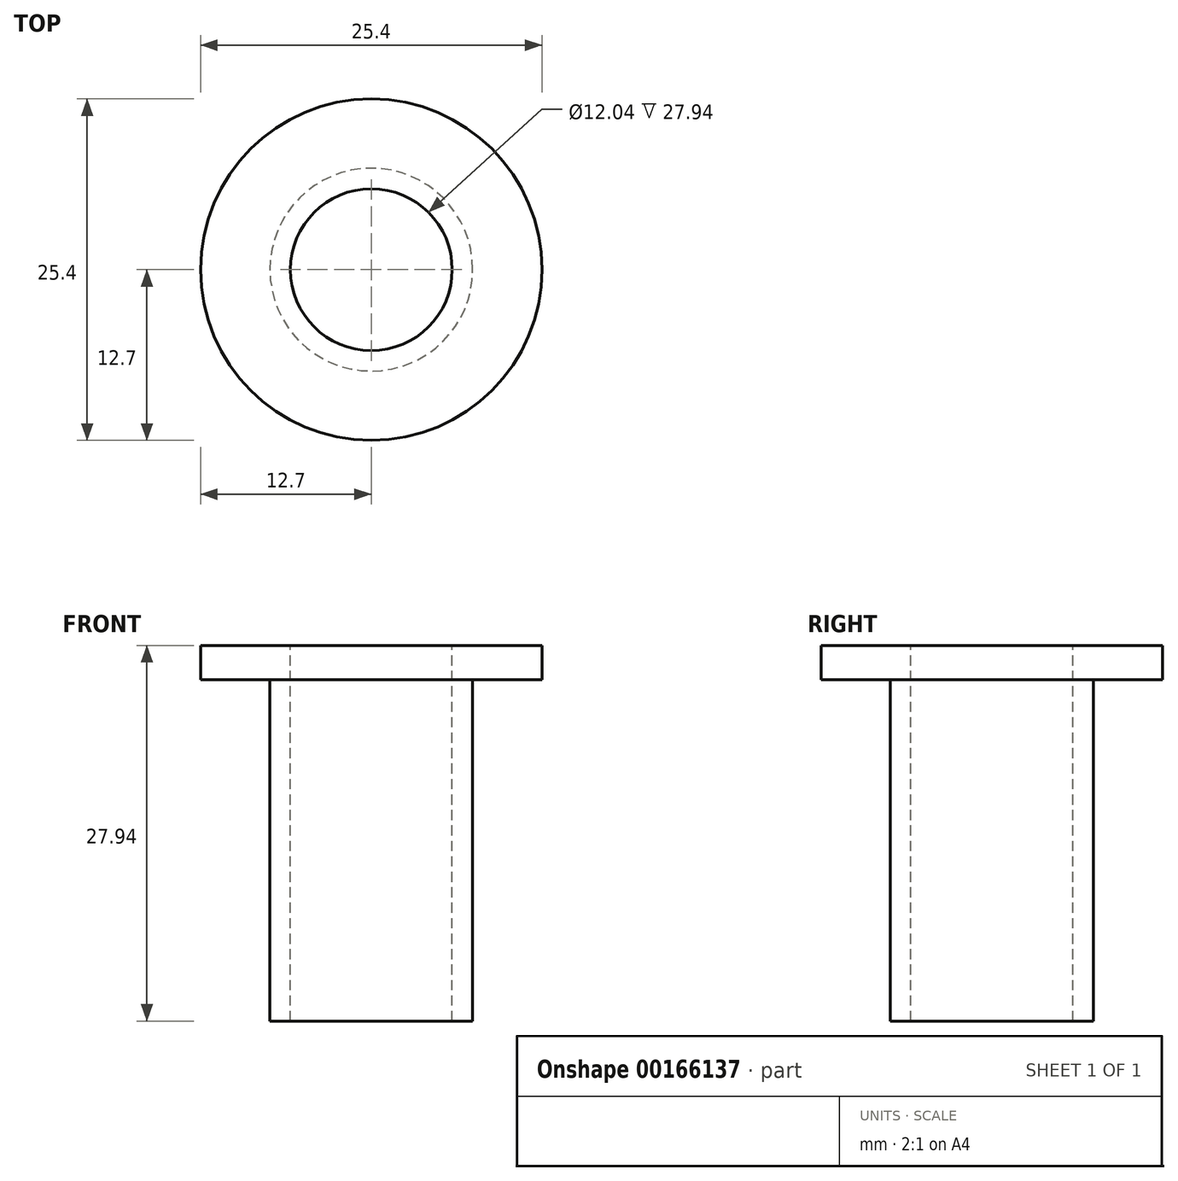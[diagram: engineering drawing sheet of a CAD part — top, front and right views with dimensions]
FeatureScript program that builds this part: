
annotation { "Feature Type Name" : "Feature", "Feature Type Description" : "" }
export const myFeature = defineFeature(function(context is Context, id is Id, definition is map)
    precondition{}
    {
        {
            var Q0;
            Q0=qCreatedBy(makeId("Front.planeOp"),FACE);
            var sketch = newSketch(context, id + "F0", { "sketchPlane" : qUnion([Q0])});
            skLineSegment(sketch, "E0", {"start": v(7.54, 0) * mm, "end": v(7.54, -25.4) * mm});
            skLineSegment(sketch, "E1", {"start": v(7.54, -25.4) * mm, "end": v(6.02, -25.4) * mm});
            skLineSegment(sketch, "E2", {"start": v(6.02, -25.4) * mm, "end": v(6.02, 2.54) * mm});
            skLineSegment(sketch, "E3", {"start": v(6.02, 2.54) * mm, "end": v(12.7, 2.54) * mm});
            skLineSegment(sketch, "E4", {"start": v(12.7, 2.54) * mm, "end": v(12.7, 0) * mm});
            skLineSegment(sketch, "E5", {"start": v(12.7, 0) * mm, "end": v(7.54, 0) * mm});
            skLineSegment(sketch, "E6", {"start": v(0, 11.06) * mm, "end": v(0, -18.55) * mm, "construction": true});
            skPoint(sketch, "E7.visualSharp", {"position": v(12.7, 2.54) * mm});
            skSolve(sketch);
        }
        {
            var Q0;
            Q0 = qSketchRegion(id + "F0", true);
            var Q1;
            Q1=sQuery(id+"F0.wireOp",EDGE,"E6");
            revolve(context, id + "F1", {"entities" : qUnion([Q0]), "axis" : qUnion([Q1]), "revolveType" : RevolveType.FULL});
        }
    });
